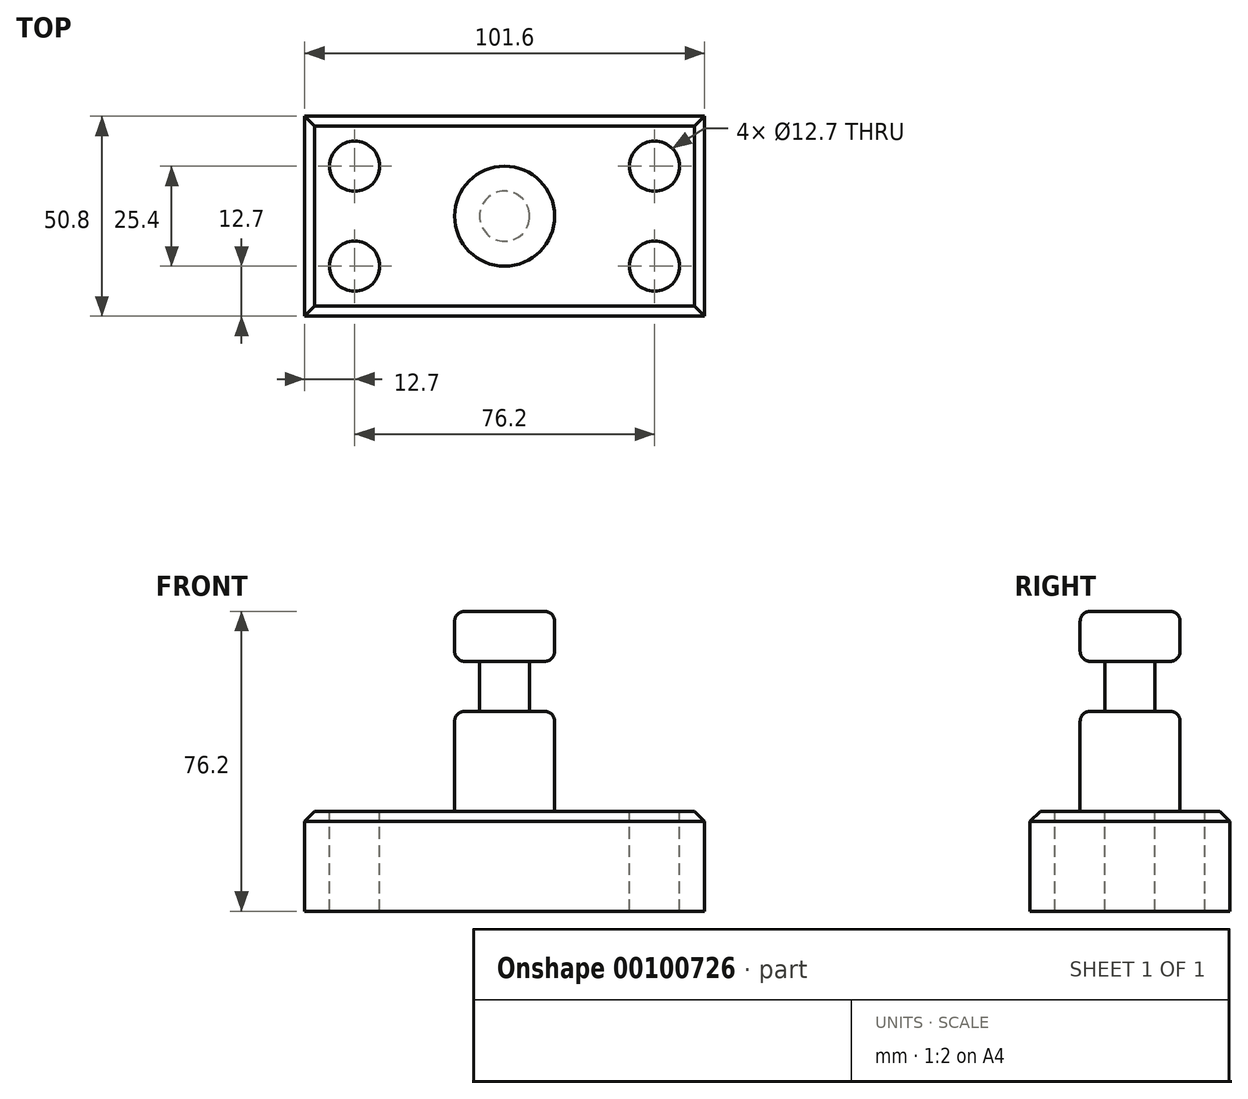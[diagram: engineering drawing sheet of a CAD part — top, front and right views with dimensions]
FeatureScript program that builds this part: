
annotation { "Feature Type Name" : "Feature", "Feature Type Description" : "" }
export const myFeature = defineFeature(function(context is Context, id is Id, definition is map)
    precondition{}
    {
        {
            var Q0;
            Q0=qCreatedBy(makeId("Top.planeOp"),FACE);
            var sketch = newSketch(context, id + "F0", { "sketchPlane" : qUnion([Q0])});
            skLineSegment(sketch, "E0.bottom", {"start": v(50.8, -25.4) * mm, "end": v(-50.8, -25.4) * mm});
            skLineSegment(sketch, "E0.top", {"start": v(50.8, 25.4) * mm, "end": v(-50.8, 25.4) * mm});
            skLineSegment(sketch, "E0.left", {"start": v(50.8, -25.4) * mm, "end": v(50.8, 25.4) * mm});
            skLineSegment(sketch, "E0.right", {"start": v(-50.8, -25.4) * mm, "end": v(-50.8, 25.4) * mm});
            skPoint(sketch, "E0.middle", {"position": v(0, 0) * mm});
            skSolve(sketch);
        }
        {
            var Q0;
            Q0=makeQuery(id+"F0.imprint","IMPRINT",FACE,{"disambiguationData":[TD([[makeQuery(id+"F0.imprint","IMPRINT",EDGE,{"derivedFrom":sQuery(id+"F0.wireOp",EDGE,"E0.bottom")}),-1.0]])]});
            extrude(context, id + "F1", {"entities" : qUnion([Q0]), "depth" : 25.4 * mm});
        }
        {
            var Q0;
            Q0=makeQuery(id+"F1.opExtrude","CAP_FACE",FACE,{"disambiguationData":[OSD([sQuery(id+"F0.wireOp",EDGE,"E0.bottom"),sQuery(id+"F0.wireOp",EDGE,"E0.top"),sQuery(id+"F0.wireOp",EDGE,"E0.left"),sQuery(id+"F0.wireOp",EDGE,"E0.right")])],"isStart":false});
            var sketch = newSketch(context, id + "F2", { "sketchPlane" : qUnion([Q0])});
            skCircle(sketch, "E1", {"center": v(-38.1, 12.7) * mm, "radius": 6.35 * mm});
            skCircle(sketch, "E2", {"center": v(38.1, 12.7) * mm, "radius": 6.35 * mm});
            skCircle(sketch, "E3", {"center": v(38.1, -12.7) * mm, "radius": 6.35 * mm});
            skCircle(sketch, "E4", {"center": v(-38.1, -12.7) * mm, "radius": 6.35 * mm});
            skSolve(sketch);
        }
        {
            var Q0;
            Q0=makeQuery(id+"F2.imprint","IMPRINT",FACE,{"disambiguationData":[TD([[makeQuery(id+"F2.imprint","IMPRINT",EDGE,{"derivedFrom":sQuery(id+"F2.wireOp",EDGE,"E3")}),1.0]])]});
            var Q1;
            Q1=makeQuery(id+"F2.imprint","IMPRINT",FACE,{"disambiguationData":[TD([[makeQuery(id+"F2.imprint","IMPRINT",EDGE,{"derivedFrom":sQuery(id+"F2.wireOp",EDGE,"E2")}),1.0]])]});
            var Q2;
            Q2=makeQuery(id+"F2.imprint","IMPRINT",FACE,{"disambiguationData":[TD([[makeQuery(id+"F2.imprint","IMPRINT",EDGE,{"derivedFrom":sQuery(id+"F2.wireOp",EDGE,"E1")}),1.0]])]});
            var Q3;
            Q3=makeQuery(id+"F2.imprint","IMPRINT",FACE,{"disambiguationData":[TD([[makeQuery(id+"F2.imprint","IMPRINT",EDGE,{"derivedFrom":sQuery(id+"F2.wireOp",EDGE,"E4")}),1.0]])]});
            extrude(context, id + "F3", {"entities" : qUnion([Q0, Q1, Q2, Q3]), "operationType" : NewBodyOperationType.REMOVE, "endBound" : BoundingType.THROUGH_ALL, "oppositeDirection" : true, "depth" : 25.4 * mm});
        }
        {
            var Q0;
            Q0=qCreatedBy(makeId("Front.planeOp"),FACE);
            var sketch = newSketch(context, id + "F4", { "sketchPlane" : qUnion([Q0])});
            skLineSegment(sketch, "E5.bottom", {"start": v(0, 25.4) * mm, "end": v(-12.7, 25.4) * mm});
            skLineSegment(sketch, "E5.top", {"start": v(0, 76.2) * mm, "end": v(-12.7, 76.2) * mm});
            skLineSegment(sketch, "E5.left", {"start": v(0, 25.4) * mm, "end": v(0, 76.2) * mm});
            skLineSegment(sketch, "E5.right", {"start": v(-12.7, 25.4) * mm, "end": v(-12.7, 76.2) * mm});
            skSolve(sketch);
        }
        {
            var Q0;
            Q0 = qSketchRegion(id + "F4", true);
            var Q1;
            Q1=sQuery(id+"F4.wireOp",EDGE,"E5.left");
            revolve(context, id + "F5", {"operationType" : NewBodyOperationType.ADD, "entities" : qUnion([Q0]), "axis" : qUnion([Q1]), "revolveType" : RevolveType.FULL});
        }
        {
            var Q0;
            Q0=qCreatedBy(makeId("Front.planeOp"),FACE);
            var sketch = newSketch(context, id + "F6", { "sketchPlane" : qUnion([Q0])});
            skLineSegment(sketch, "E6.bottom", {"start": v(-6.35, 63.5) * mm, "end": v(-25.31, 63.5) * mm});
            skLineSegment(sketch, "E6.top", {"start": v(-6.35, 50.8) * mm, "end": v(-25.31, 50.8) * mm});
            skLineSegment(sketch, "E6.left", {"start": v(-6.35, 63.5) * mm, "end": v(-6.35, 50.8) * mm});
            skLineSegment(sketch, "E6.right", {"start": v(-25.31, 63.5) * mm, "end": v(-25.31, 50.8) * mm});
            skLineSegment(sketch, "E7", {"start": v(0, 0) * mm, "end": v(0, 93.29) * mm, "construction": true});
            skSolve(sketch);
        }
        {
            var Q0;
            Q0=makeQuery(id+"F6.imprint","IMPRINT",FACE,{"disambiguationData":[TD([[makeQuery(id+"F6.imprint","IMPRINT",EDGE,{"derivedFrom":sQuery(id+"F6.wireOp",EDGE,"E6.bottom")}),1.0]])]});
            var Q1;
            Q1=sQuery(id+"F6.wireOp",EDGE,"E7");
            revolve(context, id + "F7", {"operationType" : NewBodyOperationType.REMOVE, "entities" : qUnion([Q0]), "axis" : qUnion([Q1]), "revolveType" : RevolveType.FULL, "oppositeDirection" : true});
        }
        {
            var Q0;
            Q0=makeQuery(id+"F7.boolean.opBoolean","INTERSECT",EDGE,{"derivedFrom":[makeQuery(id+"F5.opRevolve","SWEPT_FACE",FACE,{"disambiguationData":[OSD([sQuery(id+"F4.wireOp",EDGE,"E5.right")])]}),makeQuery(id+"F7.opRevolve","SWEPT_FACE",FACE,{"disambiguationData":[OSD([sQuery(id+"F6.wireOp",EDGE,"E6.top")])]})]});
            var Q1;
            Q1=makeQuery(id+"F5.opRevolve","SWEPT_EDGE",EDGE,{"disambiguationData":[OSD([sQuery(id+"F4.wireOp",EDGE,"E5.top"),sQuery(id+"F4.wireOp",EDGE,"E5.right")])]});
            var Q2;
            Q2=makeQuery(id+"F5.opRevolve","SWEPT_EDGE",EDGE,{"disambiguationData":[OSD([sQuery(id+"F4.wireOp",EDGE,"E5.bottom"),sQuery(id+"F4.wireOp",EDGE,"E5.right")])]});
            var Q3;
            Q3=makeQuery(id+"F7.boolean.opBoolean","INTERSECT",EDGE,{"derivedFrom":[makeQuery(id+"F5.opRevolve","SWEPT_FACE",FACE,{"disambiguationData":[OSD([sQuery(id+"F4.wireOp",EDGE,"E5.right")])]}),makeQuery(id+"F7.opRevolve","SWEPT_FACE",FACE,{"disambiguationData":[OSD([sQuery(id+"F6.wireOp",EDGE,"E6.bottom")])]})]});
            fillet(context, id + "F8", {"entities" : qUnion([Q0, Q1, Q2, Q3]), "radius" : 2.54 * mm, "tangentPropagation" : true, "allowEdgeOverflow" : false});
        }
        {
            var Q0;
            Q0=makeQuery(id+"F1.opExtrude","CAP_EDGE",EDGE,{"disambiguationData":[OSD([sQuery(id+"F0.wireOp",EDGE,"E0.top")])],"isStart":false});
            var Q1;
            Q1=makeQuery(id+"F1.opExtrude","CAP_EDGE",EDGE,{"disambiguationData":[OSD([sQuery(id+"F0.wireOp",EDGE,"E0.left")])],"isStart":false});
            var Q2;
            Q2=makeQuery(id+"F1.opExtrude","CAP_EDGE",EDGE,{"disambiguationData":[OSD([sQuery(id+"F0.wireOp",EDGE,"E0.bottom")])],"isStart":false});
            var Q3;
            Q3=makeQuery(id+"F1.opExtrude","CAP_EDGE",EDGE,{"disambiguationData":[OSD([sQuery(id+"F0.wireOp",EDGE,"E0.right")])],"isStart":false});
            chamfer(context, id + "F9", {"entities" : qUnion([Q0, Q1, Q2, Q3]), "width" : 2.54 * mm, "tangentPropagation" : true});
        }
    });
